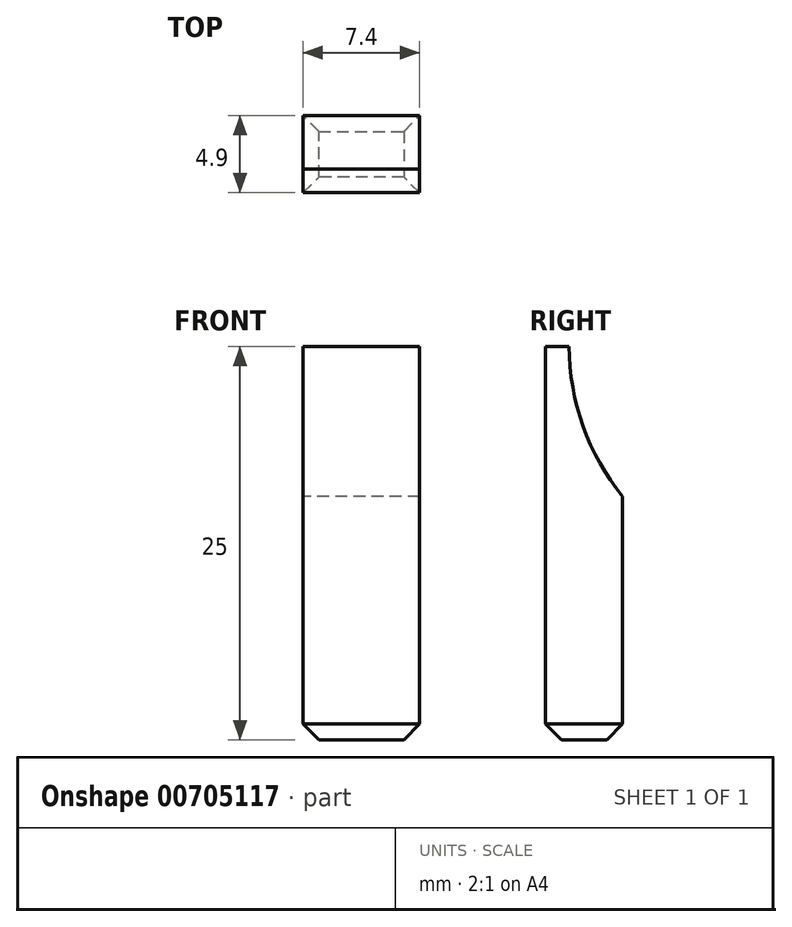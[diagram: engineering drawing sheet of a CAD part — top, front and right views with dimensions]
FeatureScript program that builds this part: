
annotation { "Feature Type Name" : "Feature", "Feature Type Description" : "" }
export const myFeature = defineFeature(function(context is Context, id is Id, definition is map)
    precondition{}
    {
        {
            var Q0;
            Q0=qCreatedBy(makeId("Right.planeOp"),FACE);
            var sketch = newSketch(context, id + "F0", { "sketchPlane" : qUnion([Q0])});
            skLineSegment(sketch, "E0", {"start": v(0, 0) * mm, "end": v(0, -9.8) * mm});
            skLineSegment(sketch, "E1", {"start": v(0, -9.8) * mm, "end": v(-4.9, -9.8) * mm});
            skLineSegment(sketch, "E2", {"start": v(-4.9, -9.8) * mm, "end": v(-4.9, 15.2) * mm});
            skArc(sketch, "E3", {"start": v(11.85, 0) * mm, "mid": v(1.08, 4.45) * mm, "end": v(-3.4, 15.2) * mm});
            skLineSegment(sketch, "E4", {"start": v(0, 0) * mm, "end": v(11.85, 0) * mm, "construction": true});
            skLineSegment(sketch, "E5", {"start": v(11.85, 0) * mm, "end": v(11.85, 15.25) * mm, "construction": true});
            skLineSegment(sketch, "E6", {"start": v(-4.9, 15.2) * mm, "end": v(-3.4, 15.2) * mm});
            skLineSegment(sketch, "E7", {"start": v(0, 0) * mm, "end": v(0, 5.65) * mm});
            skSolve(sketch);
        }
        {
            var Q0;
            Q0=makeQuery(id+"F0.imprint","IMPRINT",FACE,{"disambiguationData":[TD([[makeQuery(id+"F0.imprint","IMPRINT",EDGE,{"derivedFrom":sQuery(id+"F0.wireOp",EDGE,"E0")}),-1.0]])]});
            extrude(context, id + "F1", {"entities" : qUnion([Q0]), "endBound" : BoundingType.SYMMETRIC, "depth" : 7.4 * mm, "offsetDistance" : 25 * mm});
        }
        {
            var Q0;
            Q0=makeQuery(id+"F1.opExtrude","SWEPT_EDGE",EDGE,{"disambiguationData":[OSD([sQuery(id+"F0.wireOp",EDGE,"E1"),sQuery(id+"F0.wireOp",EDGE,"E2")])]});
            var Q1;
            Q1=makeQuery(id+"F1.opExtrude","SWEPT_EDGE",EDGE,{"disambiguationData":[OSD([sQuery(id+"F0.wireOp",EDGE,"E0"),sQuery(id+"F0.wireOp",EDGE,"E1")])]});
            var Q2;
            Q2=makeQuery(id+"F1.opExtrude","CAP_EDGE",EDGE,{"disambiguationData":[OSD([sQuery(id+"F0.wireOp",EDGE,"E1")])],"isStart":false});
            var Q3;
            Q3=makeQuery(id+"F1.opExtrude","CAP_EDGE",EDGE,{"disambiguationData":[OSD([sQuery(id+"F0.wireOp",EDGE,"E1")])],"isStart":true});
            chamfer(context, id + "F2", {"entities" : qUnion([Q0, Q1, Q2, Q3]), "width" : 1 * mm, "tangentPropagation" : true});
        }
    });
